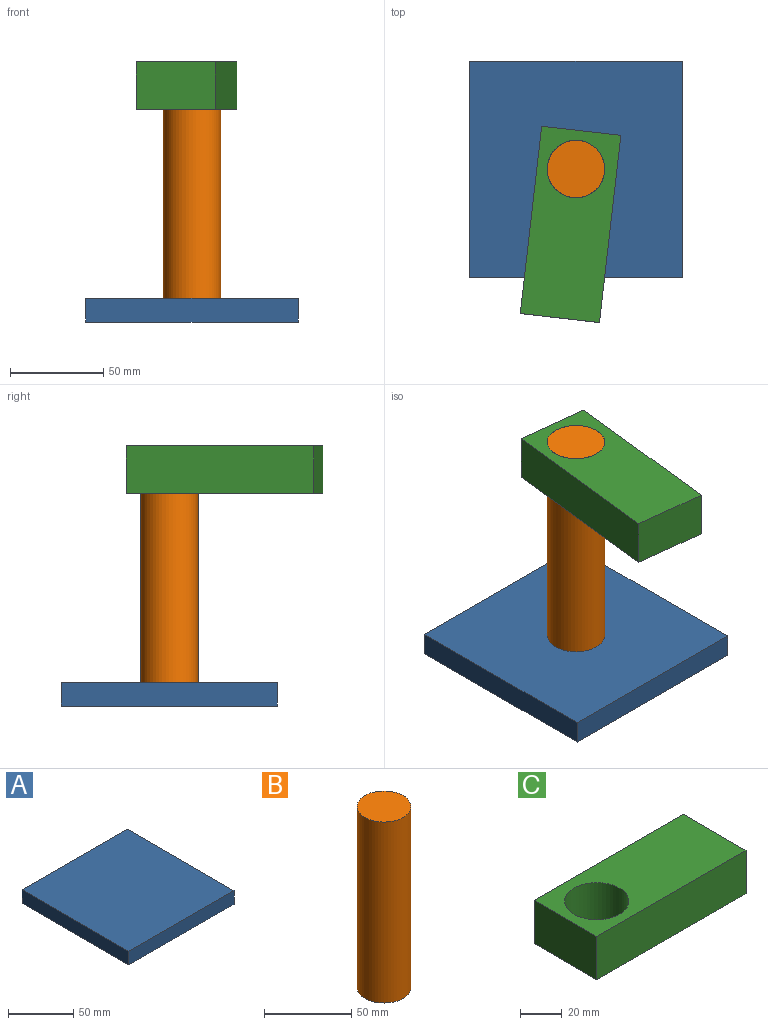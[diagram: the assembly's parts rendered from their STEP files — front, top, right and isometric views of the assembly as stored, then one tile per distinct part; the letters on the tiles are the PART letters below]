
ASSEMBLY  parts=3 mates=2
PART A: 6 faces, bbox 114.1x116.1x12.7 mm
  f0: plane 116.06x12.7mm, normal (-1,0,0), area 1474mm2, adj f1,f3,f4,f5
  f1: plane 114.1x12.7mm, normal (0,-1,0), area 1449mm2, adj f0,f2,f4,f5
  f2: plane 116.06x12.7mm, normal (1,0,0), area 1474mm2, adj f1,f3,f4,f5
  f3: plane 114.1x12.7mm, normal (0,1,0), area 1449mm2, adj f0,f2,f4,f5
  f4: plane 116.06x114.1mm, normal (0,0,1), area 13242.3mm2, adj f0,f1,f2,f3
  f5: plane 116.06x114.1mm, normal (0,0,-1), area 13242.3mm2, adj f0,f1,f2,f3
PART B: 3 faces, bbox 30.9x30.9x127 mm
  f0: cylinder r=15.44mm len=127mm, axis (0,0,-1), area 12317.8mm2, adj f1,f2
  f1: plane 30.87x30.87mm, normal (0,0,1), area 748.6mm2, adj f0
  f2: plane 30.87x30.87mm, normal (0,0,-1), area 748.6mm2, adj f0
PART C: 7 faces, bbox 101.2x42.8x25.4 mm
  f0: plane 42.8x25.4mm, normal (-1,0,0), area 1087mm2, adj f1,f4,f5,f6
  f1: plane 101.22x25.4mm, normal (0,-1,0), area 2571mm2, adj f0,f2,f5,f6
  f2: plane 42.8x25.4mm, normal (1,0,0), area 1087mm2, adj f1,f4,f5,f6
  f3: cylinder r=15.44mm len=30.87mm, axis (0,0,-1), area 2463.6mm2, adj f5,f6
  f4: plane 101.22x25.4mm, normal (0,1,0), area 2571mm2, adj f0,f2,f5,f6
  f5: plane 101.22x42.8mm, normal (0,0,1), area 3583.3mm2, adj f0,f1,f2,f3,f4
  f6: plane 101.22x42.8mm, normal (0,0,-1), area 3583.3mm2, adj f0,f1,f2,f3,f4
PLACE A t=(27.47,-8.58,-106.65)mm fixed
PLACE B rot(axis=(0,0,1),180deg) t=(27.47,-8.58,-93.95)mm
PLACE C rot(axis=(0,0,-1),96.5deg) t=(27.47,-8.58,-119.35)mm
MATE fastened A.f4 <-> B.f0  axis (0,0,1) through (27.47,-8.58,-93.95)mm
MATE revolute C.f3 <-> B.f0  axis (0,0,-1) through (27.47,-8.58,33.05)mm
